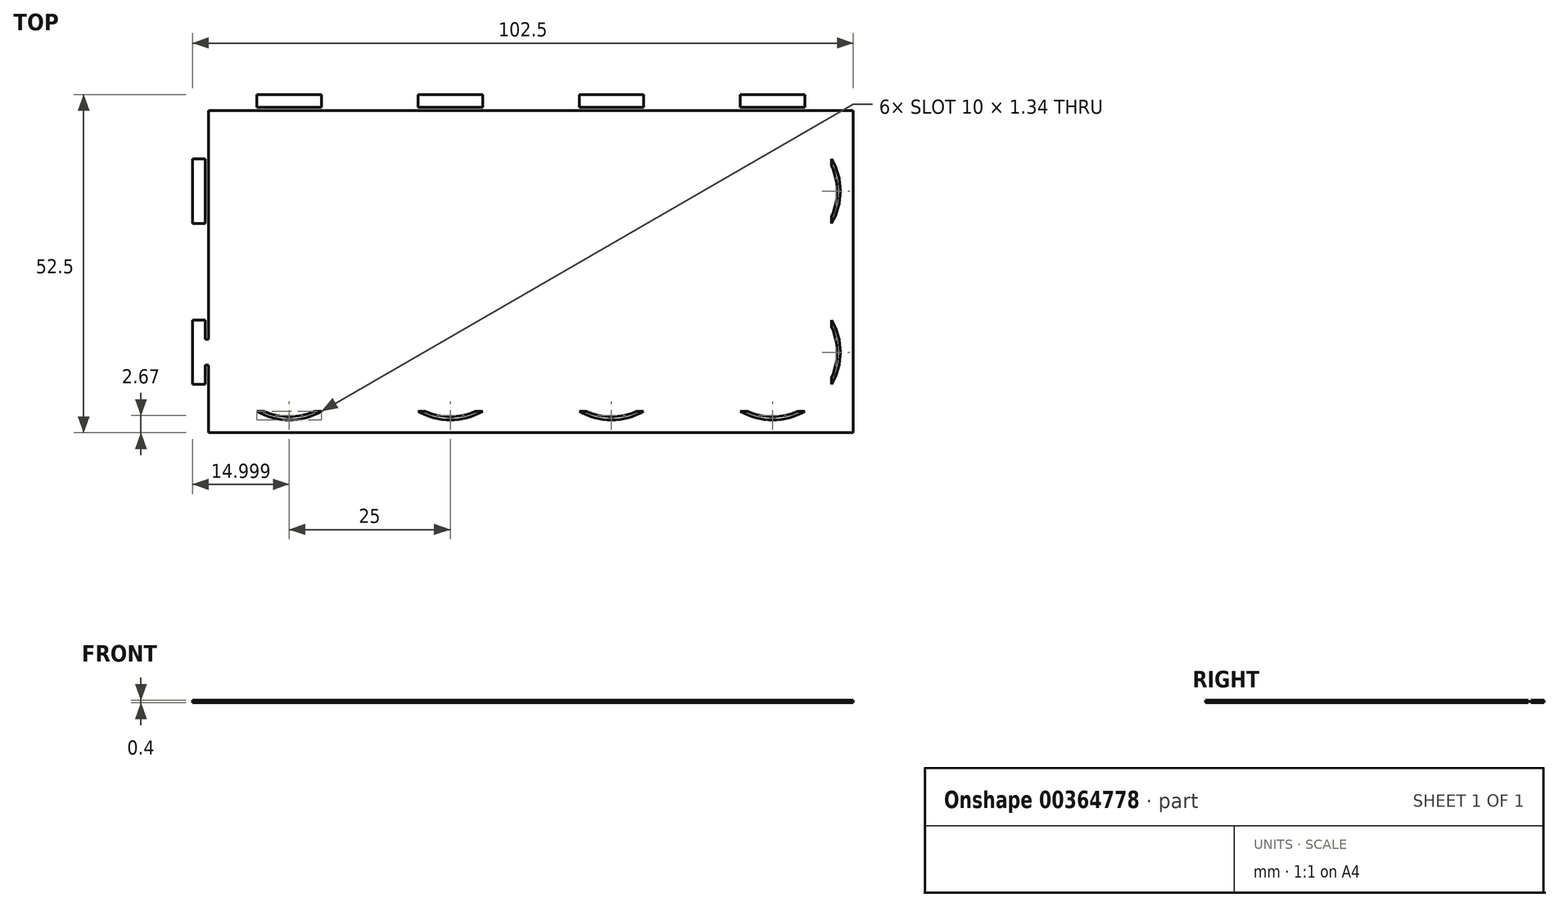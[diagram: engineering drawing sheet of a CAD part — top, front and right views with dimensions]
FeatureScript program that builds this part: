
annotation { "Feature Type Name" : "Feature", "Feature Type Description" : "" }
export const myFeature = defineFeature(function(context is Context, id is Id, definition is map)
    precondition{}
    {
        {
            var Q0;
            Q0=qCreatedBy(makeId("Top.planeOp"),FACE);
            var sketch = newSketch(context, id + "F0", { "sketchPlane" : qUnion([Q0])});
            skLineSegment(sketch, "E0.bottom", {"start": v(-73.43, 37.5) * mm, "end": v(26.57, 37.5) * mm});
            skLineSegment(sketch, "E0.top", {"start": v(-73.43, -12.5) * mm, "end": v(26.57, -12.5) * mm});
            skLineSegment(sketch, "E0.left", {"start": v(-73.43, 37.5) * mm, "end": v(-73.43, -12.5) * mm});
            skLineSegment(sketch, "E0.right", {"start": v(26.57, 37.5) * mm, "end": v(26.57, -12.5) * mm});
            skLineSegment(sketch, "E1.bottom", {"start": v(-58.93, 37.5) * mm, "end": v(-62.93, 37.5) * mm});
            skLineSegment(sketch, "E1.top", {"start": v(-58.93, 38) * mm, "end": v(-62.93, 38) * mm});
            skLineSegment(sketch, "E1.left", {"start": v(-58.93, 37.5) * mm, "end": v(-58.93, 38) * mm});
            skLineSegment(sketch, "E1.right", {"start": v(-62.93, 37.5) * mm, "end": v(-62.93, 38) * mm});
            skLineSegment(sketch, "E2.bottom", {"start": v(-65.93, 40) * mm, "end": v(-55.93, 40) * mm});
            skLineSegment(sketch, "E2.top", {"start": v(-65.93, 38) * mm, "end": v(-55.93, 38) * mm});
            skLineSegment(sketch, "E2.left", {"start": v(-65.93, 40) * mm, "end": v(-65.93, 38) * mm});
            skLineSegment(sketch, "E2.right", {"start": v(-55.93, 40) * mm, "end": v(-55.93, 38) * mm});
            skPoint(sketch, "E3", {"position": v(-60.93, 38) * mm});
            skLineSegment(sketch, "E4", {"start": v(-60.93, 38) * mm, "end": v(-60.93, 37.5) * mm, "construction": true});
            skLineSegment(sketch, "E5.1.0.0", {"start": v(-40.93, 40) * mm, "end": v(-30.93, 40) * mm});
            skPoint(sketch, "E5.1.0.1", {"position": v(-35.93, 38) * mm});
            skLineSegment(sketch, "E5.1.0.2", {"start": v(-33.93, 37.5) * mm, "end": v(-37.93, 37.5) * mm});
            skLineSegment(sketch, "E5.1.0.3", {"start": v(-35.93, 38) * mm, "end": v(-35.93, 37.5) * mm, "construction": true});
            skLineSegment(sketch, "E5.1.0.4", {"start": v(-33.93, 37.5) * mm, "end": v(-33.93, 38) * mm});
            skLineSegment(sketch, "E5.1.0.5", {"start": v(-37.93, 37.5) * mm, "end": v(-37.93, 38) * mm});
            skLineSegment(sketch, "E5.1.0.6", {"start": v(-30.93, 40) * mm, "end": v(-30.93, 38) * mm});
            skLineSegment(sketch, "E5.1.0.7", {"start": v(-40.93, 40) * mm, "end": v(-40.93, 38) * mm});
            skLineSegment(sketch, "E5.1.0.8", {"start": v(-40.93, 38) * mm, "end": v(-30.93, 38) * mm});
            skLineSegment(sketch, "E5.1.0.9", {"start": v(-33.93, 38) * mm, "end": v(-37.93, 38) * mm});
            skLineSegment(sketch, "E5.2.0.0", {"start": v(-15.93, 40) * mm, "end": v(-5.93, 40) * mm});
            skPoint(sketch, "E5.2.0.1", {"position": v(-10.93, 38) * mm});
            skLineSegment(sketch, "E5.2.0.2", {"start": v(-8.93, 37.5) * mm, "end": v(-12.93, 37.5) * mm});
            skLineSegment(sketch, "E5.2.0.3", {"start": v(-10.93, 38) * mm, "end": v(-10.93, 37.5) * mm, "construction": true});
            skLineSegment(sketch, "E5.2.0.4", {"start": v(-8.93, 37.5) * mm, "end": v(-8.93, 38) * mm});
            skLineSegment(sketch, "E5.2.0.5", {"start": v(-12.93, 37.5) * mm, "end": v(-12.93, 38) * mm});
            skLineSegment(sketch, "E5.2.0.6", {"start": v(-5.93, 40) * mm, "end": v(-5.93, 38) * mm});
            skLineSegment(sketch, "E5.2.0.7", {"start": v(-15.93, 40) * mm, "end": v(-15.93, 38) * mm});
            skLineSegment(sketch, "E5.2.0.8", {"start": v(-15.93, 38) * mm, "end": v(-5.93, 38) * mm});
            skLineSegment(sketch, "E5.2.0.9", {"start": v(-8.93, 38) * mm, "end": v(-12.93, 38) * mm});
            skLineSegment(sketch, "E5.3.0.0", {"start": v(9.07, 40) * mm, "end": v(19.07, 40) * mm});
            skPoint(sketch, "E5.3.0.1", {"position": v(14.07, 38) * mm});
            skLineSegment(sketch, "E5.3.0.2", {"start": v(16.07, 37.5) * mm, "end": v(12.07, 37.5) * mm});
            skLineSegment(sketch, "E5.3.0.3", {"start": v(14.07, 38) * mm, "end": v(14.07, 37.5) * mm, "construction": true});
            skLineSegment(sketch, "E5.3.0.4", {"start": v(16.07, 37.5) * mm, "end": v(16.07, 38) * mm});
            skLineSegment(sketch, "E5.3.0.5", {"start": v(12.07, 37.5) * mm, "end": v(12.07, 38) * mm});
            skLineSegment(sketch, "E5.3.0.6", {"start": v(19.07, 40) * mm, "end": v(19.07, 38) * mm});
            skLineSegment(sketch, "E5.3.0.7", {"start": v(9.07, 40) * mm, "end": v(9.07, 38) * mm});
            skLineSegment(sketch, "E5.3.0.8", {"start": v(9.07, 38) * mm, "end": v(19.07, 38) * mm});
            skLineSegment(sketch, "E5.3.0.9", {"start": v(16.07, 38) * mm, "end": v(12.07, 38) * mm});
            skLineSegment(sketch, "E5.direction1", {"start": v(-65.93, 38) * mm, "end": v(-40.93, 38) * mm, "construction": true});
            skArc(sketch, "E6", {"start": v(-65.93, -9.16) * mm, "mid": v(-60.93, -10.5) * mm, "end": v(-55.93, -9.16) * mm});
            skArc(sketch, "E7", {"start": v(-64.84, -9.16) * mm, "mid": v(-60.93, -10) * mm, "end": v(-57.03, -9.16) * mm});
            skLineSegment(sketch, "E8", {"start": v(-65.93, -9.16) * mm, "end": v(-64.84, -9.16) * mm});
            skLineSegment(sketch, "E9.trimOffspring", {"start": v(-57.03, -9.16) * mm, "end": v(-55.93, -9.16) * mm});
            skArc(sketch, "E10.1.0.0", {"start": v(-39.84, -9.16) * mm, "mid": v(-35.93, -10) * mm, "end": v(-32.03, -9.16) * mm});
            skArc(sketch, "E10.1.0.1", {"start": v(-40.93, -9.16) * mm, "mid": v(-35.93, -10.5) * mm, "end": v(-30.93, -9.16) * mm});
            skLineSegment(sketch, "E10.1.0.2", {"start": v(-40.93, -9.16) * mm, "end": v(-39.84, -9.16) * mm});
            skLineSegment(sketch, "E10.1.0.3", {"start": v(-32.03, -9.16) * mm, "end": v(-30.93, -9.16) * mm});
            skArc(sketch, "E10.2.0.0", {"start": v(-14.84, -9.16) * mm, "mid": v(-10.93, -10) * mm, "end": v(-7.03, -9.16) * mm});
            skArc(sketch, "E10.2.0.1", {"start": v(-15.93, -9.16) * mm, "mid": v(-10.93, -10.5) * mm, "end": v(-5.93, -9.16) * mm});
            skLineSegment(sketch, "E10.2.0.2", {"start": v(-15.93, -9.16) * mm, "end": v(-14.84, -9.16) * mm});
            skLineSegment(sketch, "E10.2.0.3", {"start": v(-7.03, -9.16) * mm, "end": v(-5.93, -9.16) * mm});
            skArc(sketch, "E10.3.0.0", {"start": v(10.16, -9.16) * mm, "mid": v(14.07, -10) * mm, "end": v(17.97, -9.16) * mm});
            skArc(sketch, "E10.3.0.1", {"start": v(9.07, -9.16) * mm, "mid": v(14.07, -10.5) * mm, "end": v(19.07, -9.16) * mm});
            skLineSegment(sketch, "E10.3.0.2", {"start": v(9.07, -9.16) * mm, "end": v(10.16, -9.16) * mm});
            skLineSegment(sketch, "E10.3.0.3", {"start": v(17.97, -9.16) * mm, "end": v(19.07, -9.16) * mm});
            skLineSegment(sketch, "E10.direction1", {"start": v(-65.93, -9.16) * mm, "end": v(-40.93, -9.16) * mm, "construction": true});
            skLineSegment(sketch, "E11.bottom", {"start": v(-75.93, 5) * mm, "end": v(-73.93, 5) * mm});
            skLineSegment(sketch, "E11.top", {"start": v(-75.93, -5) * mm, "end": v(-73.93, -5) * mm});
            skLineSegment(sketch, "E11.left", {"start": v(-75.93, 5) * mm, "end": v(-75.93, -5) * mm});
            skLineSegment(sketch, "E11.right", {"start": v(-73.93, 5) * mm, "end": v(-73.93, -5) * mm});
            skPoint(sketch, "E12", {"position": v(-73.93, 0) * mm});
            skLineSegment(sketch, "E13.bottom", {"start": v(-73.93, 2) * mm, "end": v(-73.43, 2) * mm});
            skLineSegment(sketch, "E13.top", {"start": v(-73.93, -2) * mm, "end": v(-73.43, -2) * mm});
            skLineSegment(sketch, "E13.left", {"start": v(-73.93, 2) * mm, "end": v(-73.93, -2) * mm});
            skLineSegment(sketch, "E13.right", {"start": v(-73.43, 2) * mm, "end": v(-73.43, -2) * mm});
            skPoint(sketch, "E14.0.1.0", {"position": v(-73.93, 25) * mm});
            skLineSegment(sketch, "E14.0.1.1", {"start": v(-73.93, 30) * mm, "end": v(-73.93, 20) * mm});
            skLineSegment(sketch, "E14.0.1.2", {"start": v(-75.93, 30) * mm, "end": v(-75.93, 20) * mm});
            skLineSegment(sketch, "E14.0.1.3", {"start": v(-73.93, 27) * mm, "end": v(-73.93, 23) * mm});
            skLineSegment(sketch, "E14.0.1.4", {"start": v(-73.43, 27) * mm, "end": v(-73.43, 23) * mm});
            skLineSegment(sketch, "E14.0.1.5", {"start": v(-73.93, 23) * mm, "end": v(-73.43, 23) * mm});
            skLineSegment(sketch, "E14.0.1.6", {"start": v(-75.93, 30) * mm, "end": v(-73.93, 30) * mm});
            skLineSegment(sketch, "E14.0.1.7", {"start": v(-75.93, 20) * mm, "end": v(-73.93, 20) * mm});
            skLineSegment(sketch, "E14.0.1.8", {"start": v(-73.93, 27) * mm, "end": v(-73.43, 27) * mm});
            skLineSegment(sketch, "E14.direction1", {"start": v(-73.43, 2) * mm, "end": v(-74.4, 3.68) * mm, "construction": true});
            skLineSegment(sketch, "E14.direction2", {"start": v(-73.43, 2) * mm, "end": v(-73.43, 27) * mm, "construction": true});
            skLineSegment(sketch, "E15.direction1", {"start": v(9.07, -9.16) * mm, "end": v(34.07, -9.16) * mm, "construction": true});
            skArc(sketch, "E16", {"start": v(23.23, -5) * mm, "mid": v(24.57, 0) * mm, "end": v(23.23, 5) * mm});
            skArc(sketch, "E17", {"start": v(23.23, -3.9) * mm, "mid": v(24.07, 0) * mm, "end": v(23.23, 3.9) * mm});
            skLineSegment(sketch, "E18", {"start": v(23.23, -5) * mm, "end": v(23.23, -3.9) * mm});
            skLineSegment(sketch, "E19.trimOffspring", {"start": v(23.23, 3.9) * mm, "end": v(23.23, 5) * mm});
            skArc(sketch, "E20.1.0.0", {"start": v(23.23, 21.1) * mm, "mid": v(24.07, 25) * mm, "end": v(23.23, 28.9) * mm});
            skArc(sketch, "E20.1.0.1", {"start": v(23.23, 20) * mm, "mid": v(24.57, 25) * mm, "end": v(23.23, 30) * mm});
            skLineSegment(sketch, "E20.1.0.2", {"start": v(23.23, 28.9) * mm, "end": v(23.23, 30) * mm});
            skLineSegment(sketch, "E20.1.0.3", {"start": v(23.23, 20) * mm, "end": v(23.23, 21.1) * mm});
            skLineSegment(sketch, "E20.direction1", {"start": v(14.57, 0) * mm, "end": v(14.57, 25) * mm, "construction": true});
            skSolve(sketch);
        }
        {
            var Q0;
            {var subQ8=sQuery(id+"F0.wireOp",EDGE,"E0.top");Q0=makeQuery(id+"F0.imprint","IMPRINT",FACE,{"disambiguationData":[TD([[makeQuery(id+"F0.imprint","IMPRINT",EDGE,{"derivedFrom":subQ8}),1.0]])]});}
            var Q1;
            Q1=makeQuery(id+"F0.imprint","IMPRINT",FACE,{"disambiguationData":[TD([[makeQuery(id+"F0.imprint","IMPRINT",EDGE,{"derivedFrom":sQuery(id+"F0.wireOp",EDGE,"E5.3.0.0")}),-1.0]])]});
            var Q2;
            Q2=makeQuery(id+"F0.imprint","IMPRINT",FACE,{"disambiguationData":[TD([[makeQuery(id+"F0.imprint","IMPRINT",EDGE,{"derivedFrom":sQuery(id+"F0.wireOp",EDGE,"E5.3.0.2")}),-1.0]])]});
            var Q3;
            Q3=makeQuery(id+"F0.imprint","IMPRINT",FACE,{"disambiguationData":[TD([[makeQuery(id+"F0.imprint","IMPRINT",EDGE,{"derivedFrom":sQuery(id+"F0.wireOp",EDGE,"E5.1.0.0")}),-1.0]])]});
            var Q4;
            Q4=makeQuery(id+"F0.imprint","IMPRINT",FACE,{"disambiguationData":[TD([[makeQuery(id+"F0.imprint","IMPRINT",EDGE,{"derivedFrom":sQuery(id+"F0.wireOp",EDGE,"E5.2.0.0")}),-1.0]])]});
            var Q5;
            Q5=makeQuery(id+"F0.imprint","IMPRINT",FACE,{"disambiguationData":[TD([[makeQuery(id+"F0.imprint","IMPRINT",EDGE,{"derivedFrom":sQuery(id+"F0.wireOp",EDGE,"E2.bottom")}),-1.0]])]});
            var Q6;
            Q6=makeQuery(id+"F0.imprint","IMPRINT",FACE,{"disambiguationData":[TD([[makeQuery(id+"F0.imprint","IMPRINT",EDGE,{"derivedFrom":sQuery(id+"F0.wireOp",EDGE,"E5.1.0.2")}),-1.0]])]});
            var Q7;
            Q7=makeQuery(id+"F0.imprint","IMPRINT",FACE,{"disambiguationData":[TD([[makeQuery(id+"F0.imprint","IMPRINT",EDGE,{"derivedFrom":sQuery(id+"F0.wireOp",EDGE,"E5.2.0.2")}),-1.0]])]});
            var Q8;
            Q8=makeQuery(id+"F0.imprint","IMPRINT",FACE,{"disambiguationData":[TD([[makeQuery(id+"F0.imprint","IMPRINT",EDGE,{"derivedFrom":sQuery(id+"F0.wireOp",EDGE,"E1.bottom")}),-1.0]])]});
            var Q9;
            Q9=makeQuery(id+"F0.imprint","IMPRINT",FACE,{"disambiguationData":[TD([[makeQuery(id+"F0.imprint","IMPRINT",EDGE,{"derivedFrom":sQuery(id+"F0.wireOp",EDGE,"E14.0.1.2")}),1.0]])]});
            var Q10;
            {var subQ1=sQuery(id+"F0.wireOp",EDGE,"E11.bottom");Q10=makeQuery(id+"F0.imprint","IMPRINT",FACE,{"disambiguationData":[TD([[makeQuery(id+"F0.imprint","IMPRINT",EDGE,{"derivedFrom":subQ1}),-1.0]])]});}
            var Q11;
            Q11=makeQuery(id+"F0.imprint","IMPRINT",FACE,{"disambiguationData":[TD([[makeQuery(id+"F0.imprint","IMPRINT",EDGE,{"derivedFrom":sQuery(id+"F0.wireOp",EDGE,"E13.bottom")}),-1.0]])]});
            var Q12;
            Q12=makeQuery(id+"F0.imprint","IMPRINT",FACE,{"disambiguationData":[TD([[makeQuery(id+"F0.imprint","IMPRINT",EDGE,{"derivedFrom":sQuery(id+"F0.wireOp",EDGE,"E14.0.1.3")}),1.0]])]});
            extrude(context, id + "F1", {"entities" : qUnion([Q0, Q1, Q2, Q3, Q4, Q5, Q6, Q7, Q8, Q9, Q10, Q11, Q12]), "depth" : .4 * mm});
        }
    });
